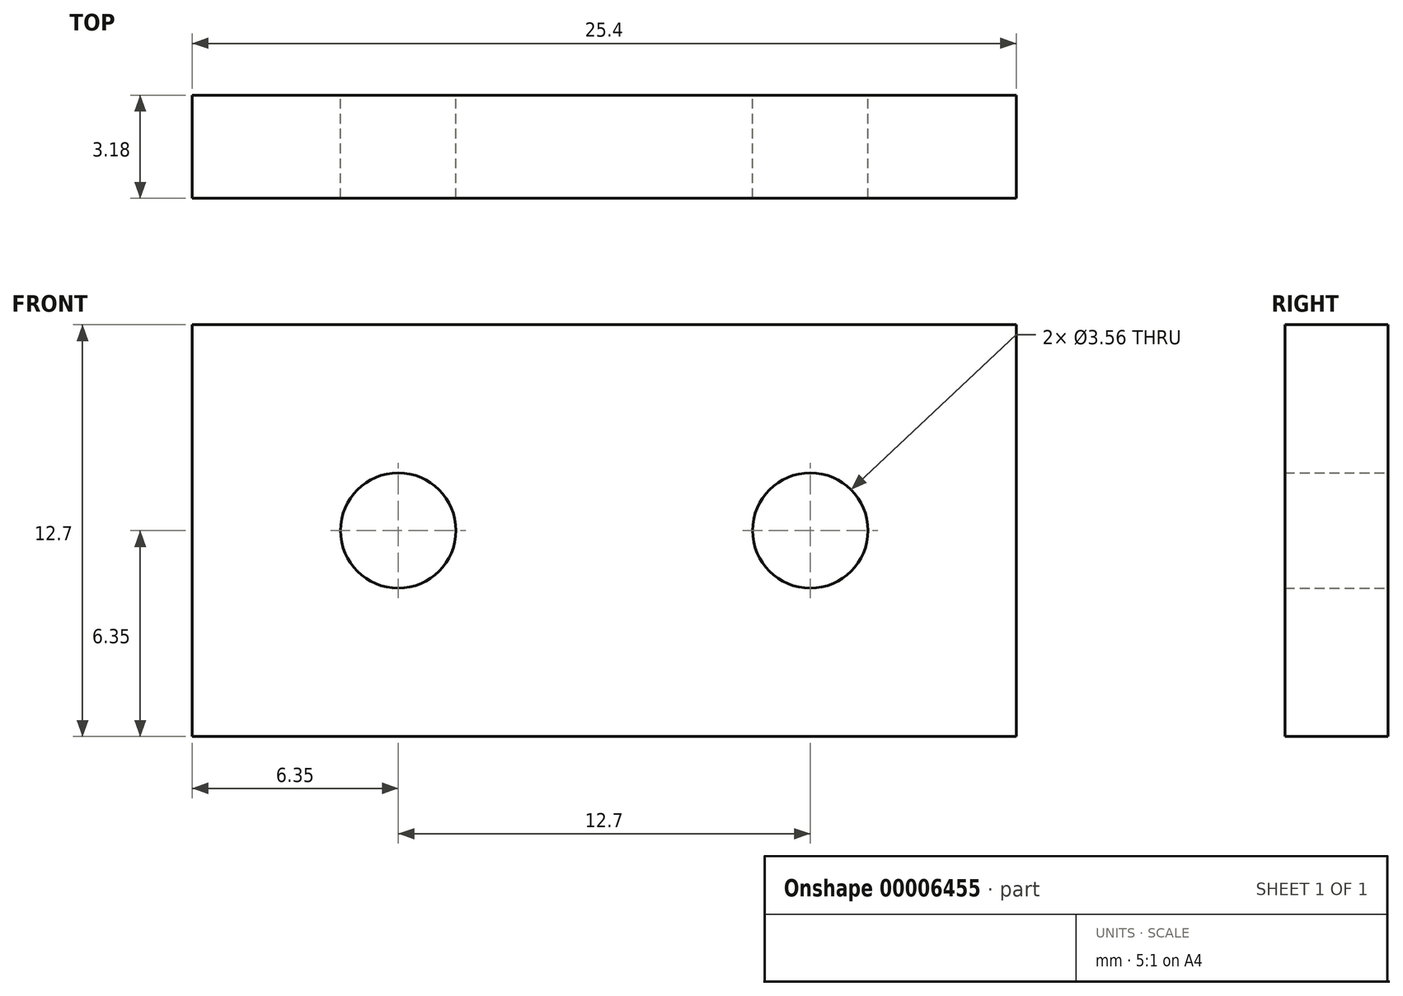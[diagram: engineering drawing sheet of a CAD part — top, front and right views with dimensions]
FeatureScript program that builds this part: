
annotation { "Feature Type Name" : "Feature", "Feature Type Description" : "" }
export const myFeature = defineFeature(function(context is Context, id is Id, definition is map)
    precondition{}
    {
        {
            var Q0;
            Q0=qCreatedBy(makeId("Front.planeOp"),FACE);
            var sketch = newSketch(context, id + "F0", { "sketchPlane" : qUnion([Q0])});
            skLineSegment(sketch, "E0.bottom", {"start": v(0, 0) * mm, "end": v(25.4, 0) * mm});
            skLineSegment(sketch, "E0.top", {"start": v(0, -12.7) * mm, "end": v(25.4, -12.7) * mm});
            skLineSegment(sketch, "E0.left", {"start": v(0, 0) * mm, "end": v(0, -12.7) * mm});
            skLineSegment(sketch, "E0.right", {"start": v(25.4, 0) * mm, "end": v(25.4, -12.7) * mm});
            skCircle(sketch, "E1", {"center": v(6.35, -6.35) * mm, "radius": 1.78 * mm});
            skCircle(sketch, "E2", {"center": v(19.05, -6.35) * mm, "radius": 1.78 * mm});
            skLineSegment(sketch, "E3", {"start": v(12.7, 0) * mm, "end": v(12.7, -12.7) * mm, "construction": true});
            skPoint(sketch, "E4", {"position": v(12.7, -6.35) * mm});
            skLineSegment(sketch, "E5", {"start": v(6.35, -6.35) * mm, "end": v(12.7, -6.35) * mm, "construction": true});
            skLineSegment(sketch, "E6", {"start": v(19.05, -6.35) * mm, "end": v(12.7, -6.35) * mm, "construction": true});
            skSolve(sketch);
        }
        {
            var Q0;
            Q0 = qSketchRegion(id + "F0", true);
            extrude(context, id + "F1", {"entities" : qUnion([Q0]), "depth" : 3.17 * mm});
        }
    });
